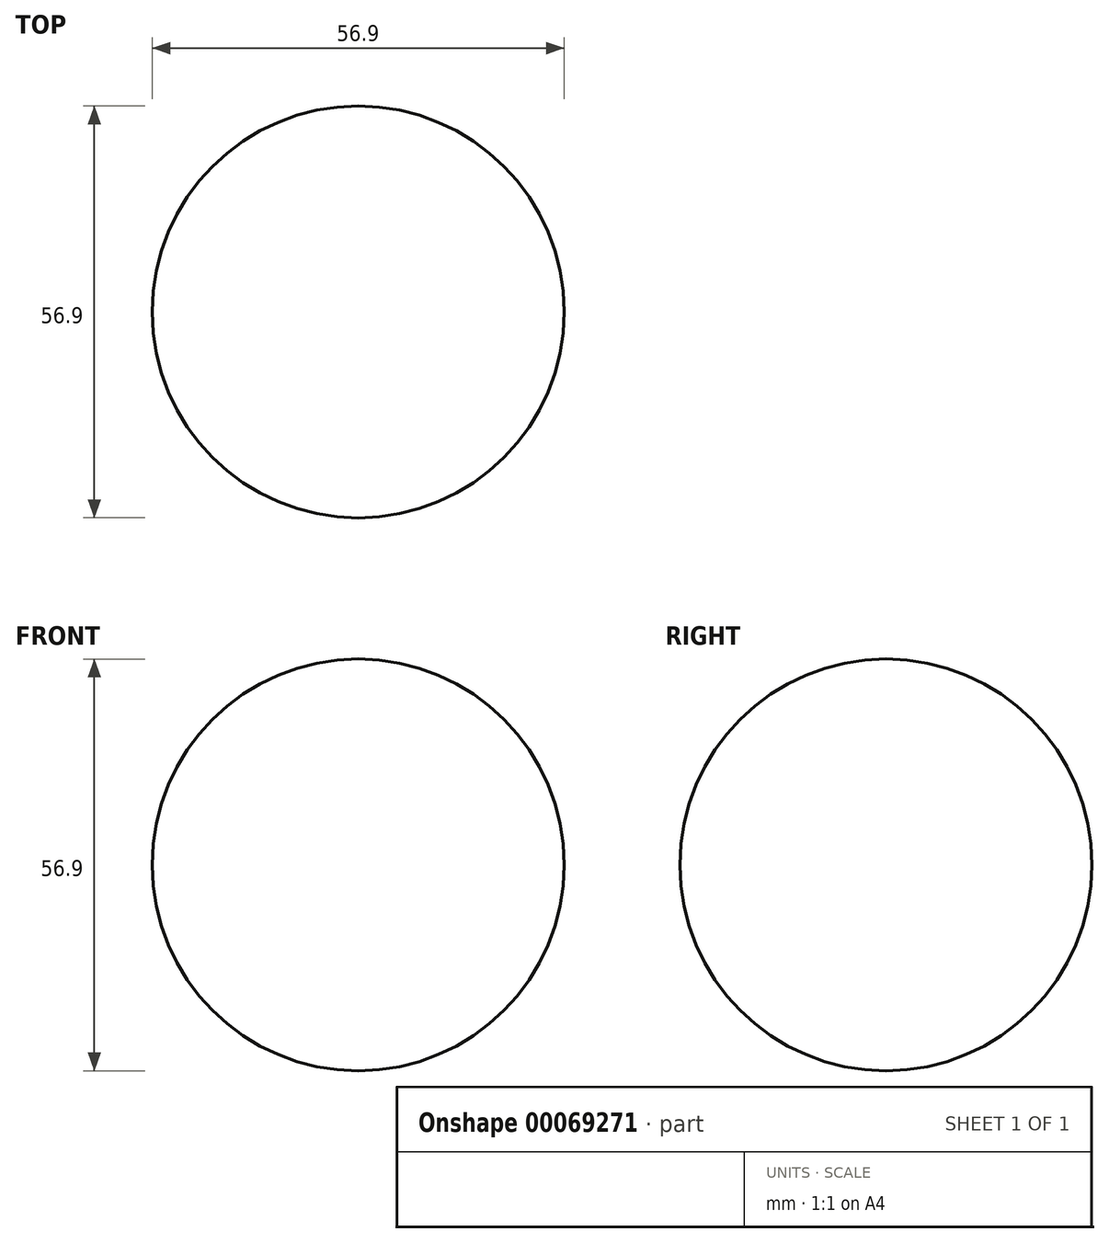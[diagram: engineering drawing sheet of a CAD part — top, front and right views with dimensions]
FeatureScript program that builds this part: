
annotation { "Feature Type Name" : "Feature", "Feature Type Description" : "" }
export const myFeature = defineFeature(function(context is Context, id is Id, definition is map)
    precondition{}
    {
        {
            var Q0;
            Q0=qCreatedBy(makeId("Front.planeOp"),FACE);
            var sketch = newSketch(context, id + "F0", { "sketchPlane" : qUnion([Q0])});
            skCircle(sketch, "E0", {"center": v(0, 0) * mm, "radius": 28.45 * mm});
            skLineSegment(sketch, "E1", {"start": v(-28.45, 0) * mm, "end": v(28.45, 0) * mm});
            skSolve(sketch);
        }
        {
            var Q0;
            {var subQ0=sQuery(id+"F0.wireOp",EDGE,"E1");Q0=makeQuery(id+"F0.imprint","IMPRINT",FACE,{"disambiguationData":[TD([[makeQuery(id+"F0.imprint","IMPRINT",EDGE,{"derivedFrom":subQ0}),1.0]])]});}
            var Q1;
            Q1=sQuery(id+"F0.wireOp",EDGE,"E1");
            revolve(context, id + "F1", {"entities" : qUnion([Q0]), "axis" : qUnion([Q1]), "revolveType" : RevolveType.FULL});
        }
    });
